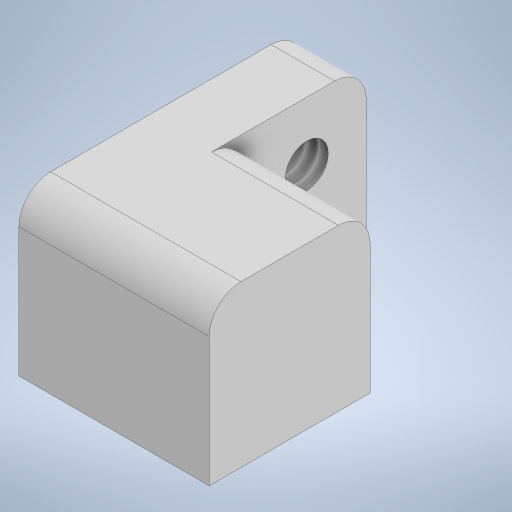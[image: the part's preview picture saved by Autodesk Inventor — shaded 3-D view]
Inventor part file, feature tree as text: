
AUTODESK INVENTOR PART (.ipt)
format: ipt  version: 2024.1 (Build 281209000, 209)  size: 246,272 bytes
history: native  units: in
note: dims shown in document units (in); Inventor stores cm internally (conversion verified against a paired STEP export)
features: sketch x5, extrude x4, projected_geometry x4, hole x1, fillet x1
ambient origin geometry x8: Origin, YZ Plane, XZ Plane, XY Plane, X Axis, Y Axis, Z Axis, Center Point
bodies: Solid1 (feature_tree)
feature tree (15):
  extrude  "Extrusion1"  Depth=0.25in
  hole  "Hole1"  [1 undecoded]
  extrude  "Extrusion2"  Depth=0.125in
  extrude  "Extrusion3"  Depth=0.0625in TaperAngle=0.0deg
  extrude  "Extrusion4"  Depth=0.0625in TaperAngle=0.0deg
  fillet  "Fillet1"  Radius=0.0079in
  sketch  "Sketch1"  dims[d0=0.125in d1=0.25in]
  sketch  "Sketch2"  dims[d2=0.375in d3=0.325in]
  sketch  "Sketch3"  dims[d4=0.325in d5=0.0in d6=0.125in]
  projected_geometry  "Projected Loop1"
  sketch  "Sketch4"  dims[d7=0.125in]
  projected_geometry  "Projected Loop2"
  sketch  "Sketch5"  dims[d8=0.0849in d9=0.224in d10=0.219in d11=0.112in d12=0.5635in d13=0.349in d14=0.8108in d15=0.0079in d16=0.0in d17=0.0079in d18=0.0in d19=0.0079in d20=0.0in d21=0.375in d22=0.0625in]
  projected_geometry  "Projected Loop3"
  projected_geometry  "Projected Loop4"
note: 1 required parameter value undecoded (feature->parameter linkage not recoverable at this tier; creation-order binding heuristic only, values carry confidence <= 0.55)
